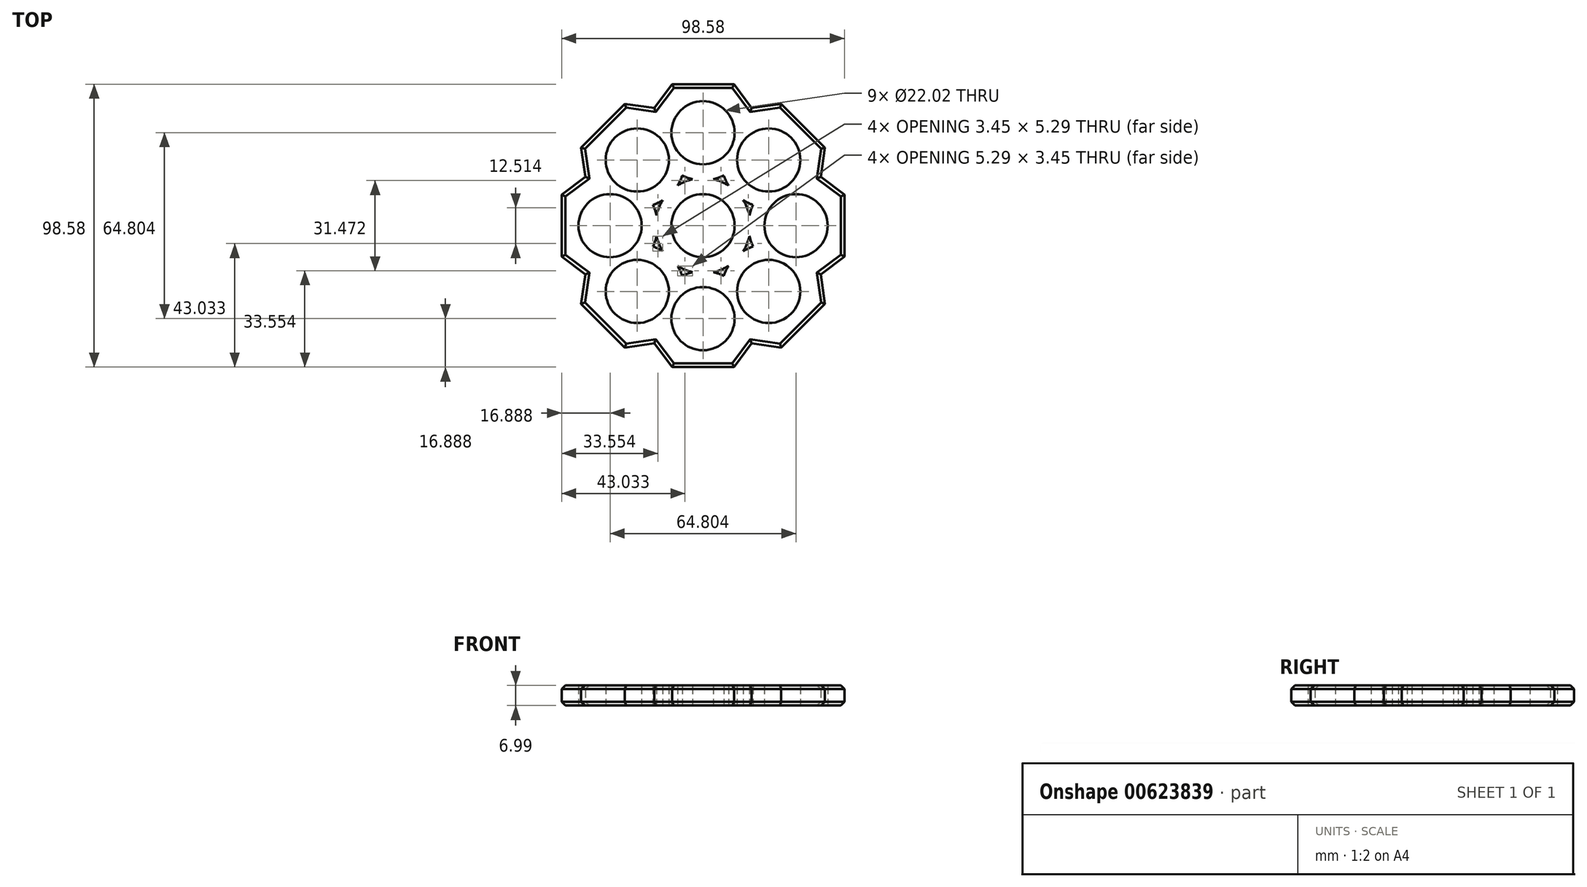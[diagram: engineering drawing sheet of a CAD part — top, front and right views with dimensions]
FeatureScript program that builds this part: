
annotation { "Feature Type Name" : "Feature", "Feature Type Description" : "" }
export const myFeature = defineFeature(function(context is Context, id is Id, definition is map)
    precondition{}
    {
        {
            var Q0;
            Q0=qCreatedBy(makeId("Top.planeOp"),FACE);
            var sketch = newSketch(context, id + "F0", { "sketchPlane" : qUnion([Q0])});
            skLineSegment(sketch, "E0", {"start": v(-9.37, 5.78) * mm, "end": v(-23.41, 32.4) * mm});
            skLineSegment(sketch, "E1", {"start": v(-23.41, 32.4) * mm, "end": v(-10.8, 49.3) * mm});
            skLineSegment(sketch, "E2", {"start": v(-10.8, 49.3) * mm, "end": v(10.8, 49.3) * mm});
            skLineSegment(sketch, "E3", {"start": v(10.8, 49.3) * mm, "end": v(23.41, 32.4) * mm});
            skLineSegment(sketch, "E4", {"start": v(23.41, 32.4) * mm, "end": v(9.37, 5.78) * mm});
            skLineSegment(sketch, "E5", {"start": v(0, 49.3) * mm, "end": v(0, 32.4) * mm});
            skCircle(sketch, "E6", {"center": v(0, 0) * mm, "radius": 11.01 * mm});
            skLineSegment(sketch, "E7", {"start": v(-23.41, 32.4) * mm, "end": v(23.41, 32.4) * mm});
            skLineSegment(sketch, "E8", {"start": v(0, 32.4) * mm, "end": v(0, 0) * mm});
            skCircle(sketch, "E9", {"center": v(0, 32.4) * mm, "radius": 11.01 * mm});
            skLineSegment(sketch, "E10.1.0", {"start": v(-39.47, 6.36) * mm, "end": v(-42.49, 27.22) * mm});
            skLineSegment(sketch, "E10.1.1", {"start": v(-39.47, 6.36) * mm, "end": v(-6.36, 39.47) * mm});
            skLineSegment(sketch, "E10.1.2", {"start": v(-10.71, -2.54) * mm, "end": v(-39.47, 6.36) * mm});
            skLineSegment(sketch, "E10.1.3", {"start": v(-6.36, 39.47) * mm, "end": v(2.54, 10.71) * mm});
            skCircle(sketch, "E10.1.4", {"center": v(-22.91, 22.91) * mm, "radius": 11.01 * mm});
            skLineSegment(sketch, "E10.1.5", {"start": v(-22.91, 22.91) * mm, "end": v(0, 0) * mm});
            skLineSegment(sketch, "E10.1.6", {"start": v(-34.86, 34.86) * mm, "end": v(-22.91, 22.91) * mm});
            skLineSegment(sketch, "E10.1.7", {"start": v(-42.49, 27.22) * mm, "end": v(-27.22, 42.49) * mm});
            skLineSegment(sketch, "E10.1.8", {"start": v(-27.22, 42.49) * mm, "end": v(-6.36, 39.47) * mm});
            skLineSegment(sketch, "E10.2.0", {"start": v(-32.4, -23.41) * mm, "end": v(-49.3, -10.8) * mm});
            skLineSegment(sketch, "E10.2.1", {"start": v(-32.4, -23.41) * mm, "end": v(-32.4, 23.41) * mm});
            skLineSegment(sketch, "E10.2.2", {"start": v(-5.78, -9.37) * mm, "end": v(-32.4, -23.41) * mm});
            skLineSegment(sketch, "E10.2.3", {"start": v(-32.4, 23.41) * mm, "end": v(-5.78, 9.37) * mm});
            skCircle(sketch, "E10.2.4", {"center": v(-32.4, 0) * mm, "radius": 11.01 * mm});
            skLineSegment(sketch, "E10.2.5", {"start": v(-32.4, 0) * mm, "end": v(0, 0) * mm});
            skLineSegment(sketch, "E10.2.6", {"start": v(-49.3, 0) * mm, "end": v(-32.4, 0) * mm});
            skLineSegment(sketch, "E10.2.7", {"start": v(-49.3, -10.8) * mm, "end": v(-49.3, 10.8) * mm});
            skLineSegment(sketch, "E10.2.8", {"start": v(-49.3, 10.8) * mm, "end": v(-32.4, 23.41) * mm});
            skLineSegment(sketch, "E10.3.0", {"start": v(-6.36, -39.47) * mm, "end": v(-27.22, -42.49) * mm});
            skLineSegment(sketch, "E10.3.1", {"start": v(-6.36, -39.47) * mm, "end": v(-39.47, -6.36) * mm});
            skLineSegment(sketch, "E10.3.2", {"start": v(2.54, -10.71) * mm, "end": v(-6.36, -39.47) * mm});
            skLineSegment(sketch, "E10.3.3", {"start": v(-39.47, -6.36) * mm, "end": v(-10.71, 2.54) * mm});
            skCircle(sketch, "E10.3.4", {"center": v(-22.91, -22.91) * mm, "radius": 11.01 * mm});
            skLineSegment(sketch, "E10.3.5", {"start": v(-22.91, -22.91) * mm, "end": v(0, 0) * mm});
            skLineSegment(sketch, "E10.3.6", {"start": v(-34.86, -34.86) * mm, "end": v(-22.91, -22.91) * mm});
            skLineSegment(sketch, "E10.3.7", {"start": v(-27.22, -42.49) * mm, "end": v(-42.49, -27.22) * mm});
            skLineSegment(sketch, "E10.3.8", {"start": v(-42.49, -27.22) * mm, "end": v(-39.47, -6.36) * mm});
            skLineSegment(sketch, "E10.4.0", {"start": v(23.41, -32.4) * mm, "end": v(10.8, -49.3) * mm});
            skLineSegment(sketch, "E10.4.1", {"start": v(23.41, -32.4) * mm, "end": v(-23.41, -32.4) * mm});
            skLineSegment(sketch, "E10.4.2", {"start": v(9.37, -5.78) * mm, "end": v(23.41, -32.4) * mm});
            skLineSegment(sketch, "E10.4.3", {"start": v(-23.41, -32.4) * mm, "end": v(-9.37, -5.78) * mm});
            skCircle(sketch, "E10.4.4", {"center": v(0, -32.4) * mm, "radius": 11.01 * mm});
            skLineSegment(sketch, "E10.4.5", {"start": v(0, -32.4) * mm, "end": v(0, 0) * mm});
            skLineSegment(sketch, "E10.4.6", {"start": v(0, -49.3) * mm, "end": v(0, -32.4) * mm});
            skLineSegment(sketch, "E10.4.7", {"start": v(10.8, -49.3) * mm, "end": v(-10.8, -49.3) * mm});
            skLineSegment(sketch, "E10.4.8", {"start": v(-10.8, -49.3) * mm, "end": v(-23.41, -32.4) * mm});
            skLineSegment(sketch, "E10.5.0", {"start": v(39.47, -6.36) * mm, "end": v(42.49, -27.22) * mm});
            skLineSegment(sketch, "E10.5.1", {"start": v(39.47, -6.36) * mm, "end": v(6.36, -39.47) * mm});
            skLineSegment(sketch, "E10.5.2", {"start": v(10.71, 2.54) * mm, "end": v(39.47, -6.36) * mm});
            skLineSegment(sketch, "E10.5.3", {"start": v(6.36, -39.47) * mm, "end": v(-2.54, -10.71) * mm});
            skCircle(sketch, "E10.5.4", {"center": v(22.91, -22.91) * mm, "radius": 11.01 * mm});
            skLineSegment(sketch, "E10.5.5", {"start": v(22.91, -22.91) * mm, "end": v(0, 0) * mm});
            skLineSegment(sketch, "E10.5.6", {"start": v(34.86, -34.86) * mm, "end": v(22.91, -22.91) * mm});
            skLineSegment(sketch, "E10.5.7", {"start": v(42.49, -27.22) * mm, "end": v(27.22, -42.49) * mm});
            skLineSegment(sketch, "E10.5.8", {"start": v(27.22, -42.49) * mm, "end": v(6.36, -39.47) * mm});
            skLineSegment(sketch, "E10.6.0", {"start": v(32.4, 23.41) * mm, "end": v(49.3, 10.8) * mm});
            skLineSegment(sketch, "E10.6.1", {"start": v(32.4, 23.41) * mm, "end": v(32.4, -23.41) * mm});
            skLineSegment(sketch, "E10.6.2", {"start": v(5.78, 9.37) * mm, "end": v(32.4, 23.41) * mm});
            skLineSegment(sketch, "E10.6.3", {"start": v(32.4, -23.41) * mm, "end": v(5.78, -9.37) * mm});
            skCircle(sketch, "E10.6.4", {"center": v(32.4, 0) * mm, "radius": 11.01 * mm});
            skLineSegment(sketch, "E10.6.5", {"start": v(32.4, 0) * mm, "end": v(0, 0) * mm});
            skLineSegment(sketch, "E10.6.6", {"start": v(49.3, 0) * mm, "end": v(32.4, 0) * mm});
            skLineSegment(sketch, "E10.6.7", {"start": v(49.3, 10.8) * mm, "end": v(49.3, -10.8) * mm});
            skLineSegment(sketch, "E10.6.8", {"start": v(49.3, -10.8) * mm, "end": v(32.4, -23.41) * mm});
            skLineSegment(sketch, "E10.7.0", {"start": v(6.36, 39.47) * mm, "end": v(27.22, 42.49) * mm});
            skLineSegment(sketch, "E10.7.1", {"start": v(6.36, 39.47) * mm, "end": v(39.47, 6.36) * mm});
            skLineSegment(sketch, "E10.7.2", {"start": v(-2.54, 10.71) * mm, "end": v(6.36, 39.47) * mm});
            skLineSegment(sketch, "E10.7.3", {"start": v(39.47, 6.36) * mm, "end": v(10.71, -2.54) * mm});
            skCircle(sketch, "E10.7.4", {"center": v(22.91, 22.91) * mm, "radius": 11.01 * mm});
            skLineSegment(sketch, "E10.7.5", {"start": v(22.91, 22.91) * mm, "end": v(0, 0) * mm});
            skLineSegment(sketch, "E10.7.6", {"start": v(34.86, 34.86) * mm, "end": v(22.91, 22.91) * mm});
            skLineSegment(sketch, "E10.7.7", {"start": v(27.22, 42.49) * mm, "end": v(42.49, 27.22) * mm});
            skLineSegment(sketch, "E10.7.8", {"start": v(42.49, 27.22) * mm, "end": v(39.47, 6.36) * mm});
            skSolve(sketch);
        }
        {
            var Q0;
            {var subQ5=sQuery(id+"F0.wireOp",EDGE,"E10.1.8");var subQ7=sQuery(id+"F0.wireOp",EDGE,"E1");var subQ8=makeQuery(id+"F0.imprint","INTERSECT",VERTEX,{"derivedFrom":[subQ7,subQ5]});Q0=makeQuery(id+"F0.imprint","IMPRINT",FACE,{"disambiguationData":[TD([[makeQuery(id+"F0.imprint","IMPRINT",EDGE,{"disambiguationData":[TD([[subQ8,1.0]])],"derivedFrom":subQ7}),1.0]])]});}
            var Q1;
            {var subQ5=sQuery(id+"F0.wireOp",EDGE,"E2");var subQ6=sQuery(id+"F0.wireOp",EDGE,"E1");var subQ7=makeQuery(id+"F0.imprint","INTERSECT",VERTEX,{"derivedFrom":[subQ6,subQ5]});Q1=makeQuery(id+"F0.imprint","IMPRINT",FACE,{"disambiguationData":[TD([[makeQuery(id+"F0.imprint","IMPRINT",EDGE,{"disambiguationData":[TD([[subQ7,1.0]])],"derivedFrom":subQ6}),-1.0]])]});}
            var Q2;
            {var subQ1=sQuery(id+"F0.wireOp",EDGE,"E2");var subQ5=sQuery(id+"F0.wireOp",EDGE,"E3");var subQ6=makeQuery(id+"F0.imprint","INTERSECT",VERTEX,{"derivedFrom":[subQ1,subQ5]});Q2=makeQuery(id+"F0.imprint","IMPRINT",FACE,{"disambiguationData":[TD([[makeQuery(id+"F0.imprint","IMPRINT",EDGE,{"disambiguationData":[TD([[subQ6,1.0]])],"derivedFrom":subQ1}),-1.0]])]});}
            var Q3;
            {var subQ5=sQuery(id+"F0.wireOp",EDGE,"E3");var subQ7=sQuery(id+"F0.wireOp",EDGE,"E10.7.0");var subQ9=makeQuery(id+"F0.imprint","INTERSECT",VERTEX,{"derivedFrom":[subQ5,subQ7]});Q3=makeQuery(id+"F0.imprint","IMPRINT",FACE,{"disambiguationData":[TD([[makeQuery(id+"F0.imprint","IMPRINT",EDGE,{"disambiguationData":[TD([[subQ9,-1.0]])],"derivedFrom":subQ5}),1.0]])]});}
            var Q4;
            {var subQ5=sQuery(id+"F0.wireOp",EDGE,"E10.2.8");var subQ7=sQuery(id+"F0.wireOp",EDGE,"E10.1.0");var subQ9=makeQuery(id+"F0.imprint","INTERSECT",VERTEX,{"derivedFrom":[subQ7,subQ5]});Q4=makeQuery(id+"F0.imprint","IMPRINT",FACE,{"disambiguationData":[TD([[makeQuery(id+"F0.imprint","IMPRINT",EDGE,{"disambiguationData":[TD([[subQ9,1.0]])],"derivedFrom":subQ7}),1.0]])]});}
            var Q5;
            {var subQ0=sQuery(id+"F0.wireOp",EDGE,"E10.1.7");var subQ7=sQuery(id+"F0.wireOp",EDGE,"E10.1.0");var subQ8=makeQuery(id+"F0.imprint","INTERSECT",VERTEX,{"derivedFrom":[subQ7,subQ0]});Q5=makeQuery(id+"F0.imprint","IMPRINT",FACE,{"disambiguationData":[TD([[makeQuery(id+"F0.imprint","IMPRINT",EDGE,{"disambiguationData":[TD([[subQ8,1.0]])],"derivedFrom":subQ7}),-1.0]])]});}
            var Q6;
            {var subQ5=sQuery(id+"F0.wireOp",EDGE,"E10.3.8");var subQ7=sQuery(id+"F0.wireOp",EDGE,"E10.2.0");var subQ9=makeQuery(id+"F0.imprint","INTERSECT",VERTEX,{"derivedFrom":[subQ7,subQ5]});Q6=makeQuery(id+"F0.imprint","IMPRINT",FACE,{"disambiguationData":[TD([[makeQuery(id+"F0.imprint","IMPRINT",EDGE,{"disambiguationData":[TD([[subQ9,1.0]])],"derivedFrom":subQ7}),1.0]])]});}
            var Q7;
            {var subQ0=sQuery(id+"F0.wireOp",EDGE,"E10.2.7");var subQ7=sQuery(id+"F0.wireOp",EDGE,"E10.2.0");var subQ8=makeQuery(id+"F0.imprint","INTERSECT",VERTEX,{"derivedFrom":[subQ7,subQ0]});Q7=makeQuery(id+"F0.imprint","IMPRINT",FACE,{"disambiguationData":[TD([[makeQuery(id+"F0.imprint","IMPRINT",EDGE,{"disambiguationData":[TD([[subQ8,1.0]])],"derivedFrom":subQ7}),-1.0]])]});}
            var Q8;
            {var subQ5=sQuery(id+"F0.wireOp",EDGE,"E10.4.8");var subQ7=sQuery(id+"F0.wireOp",EDGE,"E10.3.0");var subQ9=makeQuery(id+"F0.imprint","INTERSECT",VERTEX,{"derivedFrom":[subQ7,subQ5]});Q8=makeQuery(id+"F0.imprint","IMPRINT",FACE,{"disambiguationData":[TD([[makeQuery(id+"F0.imprint","IMPRINT",EDGE,{"disambiguationData":[TD([[subQ9,1.0]])],"derivedFrom":subQ7}),1.0]])]});}
            var Q9;
            {var subQ0=sQuery(id+"F0.wireOp",EDGE,"E10.3.7");var subQ7=sQuery(id+"F0.wireOp",EDGE,"E10.3.0");var subQ8=makeQuery(id+"F0.imprint","INTERSECT",VERTEX,{"derivedFrom":[subQ7,subQ0]});Q9=makeQuery(id+"F0.imprint","IMPRINT",FACE,{"disambiguationData":[TD([[makeQuery(id+"F0.imprint","IMPRINT",EDGE,{"disambiguationData":[TD([[subQ8,1.0]])],"derivedFrom":subQ7}),-1.0]])]});}
            var Q10;
            {var subQ5=sQuery(id+"F0.wireOp",EDGE,"E10.5.8");var subQ7=sQuery(id+"F0.wireOp",EDGE,"E10.4.0");var subQ9=makeQuery(id+"F0.imprint","INTERSECT",VERTEX,{"derivedFrom":[subQ7,subQ5]});Q10=makeQuery(id+"F0.imprint","IMPRINT",FACE,{"disambiguationData":[TD([[makeQuery(id+"F0.imprint","IMPRINT",EDGE,{"disambiguationData":[TD([[subQ9,1.0]])],"derivedFrom":subQ7}),1.0]])]});}
            var Q11;
            {var subQ0=sQuery(id+"F0.wireOp",EDGE,"E10.4.7");var subQ7=sQuery(id+"F0.wireOp",EDGE,"E10.4.0");var subQ8=makeQuery(id+"F0.imprint","INTERSECT",VERTEX,{"derivedFrom":[subQ7,subQ0]});Q11=makeQuery(id+"F0.imprint","IMPRINT",FACE,{"disambiguationData":[TD([[makeQuery(id+"F0.imprint","IMPRINT",EDGE,{"disambiguationData":[TD([[subQ8,1.0]])],"derivedFrom":subQ7}),-1.0]])]});}
            var Q12;
            {var subQ5=sQuery(id+"F0.wireOp",EDGE,"E10.6.8");var subQ7=sQuery(id+"F0.wireOp",EDGE,"E10.5.0");var subQ9=makeQuery(id+"F0.imprint","INTERSECT",VERTEX,{"derivedFrom":[subQ7,subQ5]});Q12=makeQuery(id+"F0.imprint","IMPRINT",FACE,{"disambiguationData":[TD([[makeQuery(id+"F0.imprint","IMPRINT",EDGE,{"disambiguationData":[TD([[subQ9,1.0]])],"derivedFrom":subQ7}),1.0]])]});}
            var Q13;
            {var subQ0=sQuery(id+"F0.wireOp",EDGE,"E10.5.7");var subQ7=sQuery(id+"F0.wireOp",EDGE,"E10.5.0");var subQ8=makeQuery(id+"F0.imprint","INTERSECT",VERTEX,{"derivedFrom":[subQ7,subQ0]});Q13=makeQuery(id+"F0.imprint","IMPRINT",FACE,{"disambiguationData":[TD([[makeQuery(id+"F0.imprint","IMPRINT",EDGE,{"disambiguationData":[TD([[subQ8,1.0]])],"derivedFrom":subQ7}),-1.0]])]});}
            var Q14;
            {var subQ5=sQuery(id+"F0.wireOp",EDGE,"E10.7.8");var subQ7=sQuery(id+"F0.wireOp",EDGE,"E10.6.0");var subQ9=makeQuery(id+"F0.imprint","INTERSECT",VERTEX,{"derivedFrom":[subQ7,subQ5]});Q14=makeQuery(id+"F0.imprint","IMPRINT",FACE,{"disambiguationData":[TD([[makeQuery(id+"F0.imprint","IMPRINT",EDGE,{"disambiguationData":[TD([[subQ9,1.0]])],"derivedFrom":subQ7}),1.0]])]});}
            var Q15;
            {var subQ0=sQuery(id+"F0.wireOp",EDGE,"E10.6.7");var subQ7=sQuery(id+"F0.wireOp",EDGE,"E10.6.0");var subQ8=makeQuery(id+"F0.imprint","INTERSECT",VERTEX,{"derivedFrom":[subQ7,subQ0]});Q15=makeQuery(id+"F0.imprint","IMPRINT",FACE,{"disambiguationData":[TD([[makeQuery(id+"F0.imprint","IMPRINT",EDGE,{"disambiguationData":[TD([[subQ8,1.0]])],"derivedFrom":subQ7}),-1.0]])]});}
            var Q16;
            {var subQ6=sQuery(id+"F0.wireOp",EDGE,"E1");var subQ9=sQuery(id+"F0.wireOp",EDGE,"E10.1.8");var subQ11=makeQuery(id+"F0.imprint","INTERSECT",VERTEX,{"derivedFrom":[subQ6,subQ9]});Q16=makeQuery(id+"F0.imprint","IMPRINT",FACE,{"disambiguationData":[TD([[makeQuery(id+"F0.imprint","IMPRINT",EDGE,{"disambiguationData":[TD([[subQ11,1.0]])],"derivedFrom":subQ6}),-1.0]])]});}
            var Q17;
            {var subQ0=sQuery(id+"F0.wireOp",EDGE,"E10.7.0");var subQ1=sQuery(id+"F0.wireOp",EDGE,"E3");var subQ2=makeQuery(id+"F0.imprint","INTERSECT",VERTEX,{"derivedFrom":[subQ1,subQ0]});Q17=makeQuery(id+"F0.imprint","IMPRINT",FACE,{"disambiguationData":[TD([[makeQuery(id+"F0.imprint","IMPRINT",EDGE,{"disambiguationData":[TD([[subQ2,-1.0]])],"derivedFrom":subQ1}),-1.0]])]});}
            var Q18;
            {var subQ6=sQuery(id+"F0.wireOp",EDGE,"E10.1.0");var subQ9=sQuery(id+"F0.wireOp",EDGE,"E10.2.8");var subQ11=makeQuery(id+"F0.imprint","INTERSECT",VERTEX,{"derivedFrom":[subQ6,subQ9]});Q18=makeQuery(id+"F0.imprint","IMPRINT",FACE,{"disambiguationData":[TD([[makeQuery(id+"F0.imprint","IMPRINT",EDGE,{"disambiguationData":[TD([[subQ11,1.0]])],"derivedFrom":subQ6}),-1.0]])]});}
            var Q19;
            {var subQ6=sQuery(id+"F0.wireOp",EDGE,"E10.2.0");var subQ9=sQuery(id+"F0.wireOp",EDGE,"E10.3.8");var subQ11=makeQuery(id+"F0.imprint","INTERSECT",VERTEX,{"derivedFrom":[subQ6,subQ9]});Q19=makeQuery(id+"F0.imprint","IMPRINT",FACE,{"disambiguationData":[TD([[makeQuery(id+"F0.imprint","IMPRINT",EDGE,{"disambiguationData":[TD([[subQ11,1.0]])],"derivedFrom":subQ6}),-1.0]])]});}
            var Q20;
            {var subQ6=sQuery(id+"F0.wireOp",EDGE,"E10.4.0");var subQ9=sQuery(id+"F0.wireOp",EDGE,"E10.5.8");var subQ11=makeQuery(id+"F0.imprint","INTERSECT",VERTEX,{"derivedFrom":[subQ6,subQ9]});Q20=makeQuery(id+"F0.imprint","IMPRINT",FACE,{"disambiguationData":[TD([[makeQuery(id+"F0.imprint","IMPRINT",EDGE,{"disambiguationData":[TD([[subQ11,1.0]])],"derivedFrom":subQ6}),-1.0]])]});}
            var Q21;
            {var subQ6=sQuery(id+"F0.wireOp",EDGE,"E10.5.0");var subQ9=sQuery(id+"F0.wireOp",EDGE,"E10.6.8");var subQ11=makeQuery(id+"F0.imprint","INTERSECT",VERTEX,{"derivedFrom":[subQ6,subQ9]});Q21=makeQuery(id+"F0.imprint","IMPRINT",FACE,{"disambiguationData":[TD([[makeQuery(id+"F0.imprint","IMPRINT",EDGE,{"disambiguationData":[TD([[subQ11,1.0]])],"derivedFrom":subQ6}),-1.0]])]});}
            var Q22;
            {var subQ6=sQuery(id+"F0.wireOp",EDGE,"E10.6.0");var subQ9=sQuery(id+"F0.wireOp",EDGE,"E10.7.8");var subQ11=makeQuery(id+"F0.imprint","INTERSECT",VERTEX,{"derivedFrom":[subQ6,subQ9]});Q22=makeQuery(id+"F0.imprint","IMPRINT",FACE,{"disambiguationData":[TD([[makeQuery(id+"F0.imprint","IMPRINT",EDGE,{"disambiguationData":[TD([[subQ11,1.0]])],"derivedFrom":subQ6}),-1.0]])]});}
            var Q23;
            {var subQ5=sQuery(id+"F0.wireOp",EDGE,"E10.1.3");var subQ6=sQuery(id+"F0.wireOp",EDGE,"E6");var subQ7=makeQuery(id+"F0.imprint","INTERSECT",VERTEX,{"derivedFrom":[subQ6,subQ5]});Q23=makeQuery(id+"F0.imprint","IMPRINT",FACE,{"disambiguationData":[TD([[makeQuery(id+"F0.imprint","IMPRINT",EDGE,{"disambiguationData":[TD([[subQ7,1.0]])],"derivedFrom":subQ6}),-1.0]])]});}
            var Q24;
            {var subQ8=sQuery(id+"F0.wireOp",EDGE,"E6");var subQ11=sQuery(id+"F0.wireOp",EDGE,"E4");var subQ12=makeQuery(id+"F0.imprint","INTERSECT",VERTEX,{"derivedFrom":[subQ11,subQ8]});Q24=makeQuery(id+"F0.imprint","IMPRINT",FACE,{"disambiguationData":[TD([[makeQuery(id+"F0.imprint","IMPRINT",EDGE,{"disambiguationData":[TD([[subQ12,1.0]])],"derivedFrom":subQ8}),-1.0]])]});}
            var Q25;
            {var subQ12=sQuery(id+"F0.wireOp",EDGE,"E6");var subQ14=sQuery(id+"F0.wireOp",EDGE,"E10.4.2");var subQ15=makeQuery(id+"F0.imprint","INTERSECT",VERTEX,{"derivedFrom":[subQ12,subQ14]});Q25=makeQuery(id+"F0.imprint","IMPRINT",FACE,{"disambiguationData":[TD([[makeQuery(id+"F0.imprint","IMPRINT",EDGE,{"disambiguationData":[TD([[subQ15,-1.0]])],"derivedFrom":subQ12}),-1.0]])]});}
            var Q26;
            {var subQ5=sQuery(id+"F0.wireOp",EDGE,"E10.3.2");var subQ6=sQuery(id+"F0.wireOp",EDGE,"E6");var subQ7=makeQuery(id+"F0.imprint","INTERSECT",VERTEX,{"derivedFrom":[subQ6,subQ5]});Q26=makeQuery(id+"F0.imprint","IMPRINT",FACE,{"disambiguationData":[TD([[makeQuery(id+"F0.imprint","IMPRINT",EDGE,{"disambiguationData":[TD([[subQ7,-1.0]])],"derivedFrom":subQ6}),-1.0]])]});}
            var Q27;
            {var subQ5=sQuery(id+"F0.wireOp",EDGE,"E10.2.2");var subQ6=sQuery(id+"F0.wireOp",EDGE,"E6");var subQ7=makeQuery(id+"F0.imprint","INTERSECT",VERTEX,{"derivedFrom":[subQ6,subQ5]});Q27=makeQuery(id+"F0.imprint","IMPRINT",FACE,{"disambiguationData":[TD([[makeQuery(id+"F0.imprint","IMPRINT",EDGE,{"disambiguationData":[TD([[subQ7,-1.0]])],"derivedFrom":subQ6}),-1.0]])]});}
            var Q28;
            {var subQ8=sQuery(id+"F0.wireOp",EDGE,"E6");var subQ12=sQuery(id+"F0.wireOp",EDGE,"E0");var subQ13=makeQuery(id+"F0.imprint","INTERSECT",VERTEX,{"derivedFrom":[subQ12,subQ8]});Q28=makeQuery(id+"F0.imprint","IMPRINT",FACE,{"disambiguationData":[TD([[makeQuery(id+"F0.imprint","IMPRINT",EDGE,{"disambiguationData":[TD([[subQ13,-1.0]])],"derivedFrom":subQ8}),-1.0]])]});}
            var Q29;
            {var subQ5=sQuery(id+"F0.wireOp",EDGE,"E10.2.3");var subQ6=sQuery(id+"F0.wireOp",EDGE,"E6");var subQ7=makeQuery(id+"F0.imprint","INTERSECT",VERTEX,{"derivedFrom":[subQ6,subQ5]});Q29=makeQuery(id+"F0.imprint","IMPRINT",FACE,{"disambiguationData":[TD([[makeQuery(id+"F0.imprint","IMPRINT",EDGE,{"disambiguationData":[TD([[subQ7,1.0]])],"derivedFrom":subQ6}),-1.0]])]});}
            var Q30;
            {var subQ0=sQuery(id+"F0.wireOp",EDGE,"E10.2.1");var subQ1=sQuery(id+"F0.wireOp",EDGE,"E10.1.1");var subQ2=makeQuery(id+"F0.imprint","INTERSECT",VERTEX,{"derivedFrom":[subQ1,subQ0]});Q30=makeQuery(id+"F0.imprint","IMPRINT",FACE,{"disambiguationData":[TD([[makeQuery(id+"F0.imprint","IMPRINT",EDGE,{"disambiguationData":[TD([[subQ2,-1.0]])],"derivedFrom":subQ1}),1.0]])]});}
            var Q31;
            {var subQ0=sQuery(id+"F0.wireOp",EDGE,"E10.2.4");var subQ1=sQuery(id+"F0.wireOp",EDGE,"E10.1.1");var subQ2=makeQuery(id+"F0.imprint","INTERSECT",VERTEX,{"derivedFrom":[subQ1,subQ0]});Q31=makeQuery(id+"F0.imprint","IMPRINT",FACE,{"disambiguationData":[TD([[makeQuery(id+"F0.imprint","IMPRINT",EDGE,{"disambiguationData":[TD([[subQ2,-1.0]])],"derivedFrom":subQ1}),-1.0]])]});}
            var Q32;
            {var subQ0=sQuery(id+"F0.wireOp",EDGE,"E10.3.1");var subQ1=sQuery(id+"F0.wireOp",EDGE,"E10.2.1");var subQ2=makeQuery(id+"F0.imprint","INTERSECT",VERTEX,{"derivedFrom":[subQ1,subQ0]});Q32=makeQuery(id+"F0.imprint","IMPRINT",FACE,{"disambiguationData":[TD([[makeQuery(id+"F0.imprint","IMPRINT",EDGE,{"disambiguationData":[TD([[subQ2,-1.0]])],"derivedFrom":subQ1}),1.0]])]});}
            var Q33;
            {var subQ0=sQuery(id+"F0.wireOp",EDGE,"E10.1.1");var subQ1=sQuery(id+"F0.wireOp",EDGE,"E7");var subQ2=makeQuery(id+"F0.imprint","INTERSECT",VERTEX,{"derivedFrom":[subQ1,subQ0]});Q33=makeQuery(id+"F0.imprint","IMPRINT",FACE,{"disambiguationData":[TD([[makeQuery(id+"F0.imprint","IMPRINT",EDGE,{"disambiguationData":[TD([[subQ2,-1.0]])],"derivedFrom":subQ1}),1.0]])]});}
            var Q34;
            {var subQ0=sQuery(id+"F0.wireOp",EDGE,"E10.1.4");var subQ1=sQuery(id+"F0.wireOp",EDGE,"E7");var subQ2=makeQuery(id+"F0.imprint","INTERSECT",VERTEX,{"derivedFrom":[subQ1,subQ0]});Q34=makeQuery(id+"F0.imprint","IMPRINT",FACE,{"disambiguationData":[TD([[makeQuery(id+"F0.imprint","IMPRINT",EDGE,{"disambiguationData":[TD([[subQ2,-1.0]])],"derivedFrom":subQ1}),-1.0]])]});}
            var Q35;
            {var subQ0=sQuery(id+"F0.wireOp",EDGE,"E10.2.4");var subQ1=sQuery(id+"F0.wireOp",EDGE,"E10.1.2");var subQ2=makeQuery(id+"F0.imprint","INTERSECT",VERTEX,{"derivedFrom":[subQ1,subQ0]});Q35=makeQuery(id+"F0.imprint","IMPRINT",FACE,{"disambiguationData":[TD([[makeQuery(id+"F0.imprint","IMPRINT",EDGE,{"disambiguationData":[TD([[subQ2,1.0]])],"derivedFrom":subQ0}),-1.0]])]});}
            var Q36;
            {var subQ0=sQuery(id+"F0.wireOp",EDGE,"E10.2.3");var subQ1=sQuery(id+"F0.wireOp",EDGE,"E10.1.4");var subQ2=makeQuery(id+"F0.imprint","INTERSECT",VERTEX,{"derivedFrom":[subQ1,subQ0]});Q36=makeQuery(id+"F0.imprint","IMPRINT",FACE,{"disambiguationData":[TD([[makeQuery(id+"F0.imprint","IMPRINT",EDGE,{"disambiguationData":[TD([[subQ2,-1.0]])],"derivedFrom":subQ1}),-1.0]])]});}
            var Q37;
            {var subQ0=sQuery(id+"F0.wireOp",EDGE,"E10.1.4");var subQ1=sQuery(id+"F0.wireOp",EDGE,"E0");var subQ2=makeQuery(id+"F0.imprint","INTERSECT",VERTEX,{"derivedFrom":[subQ1,subQ0]});Q37=makeQuery(id+"F0.imprint","IMPRINT",FACE,{"disambiguationData":[TD([[makeQuery(id+"F0.imprint","IMPRINT",EDGE,{"disambiguationData":[TD([[subQ2,1.0]])],"derivedFrom":subQ0}),-1.0]])]});}
            var Q38;
            {var subQ0=sQuery(id+"F0.wireOp",EDGE,"E9");var subQ1=sQuery(id+"F0.wireOp",EDGE,"E8");var subQ2=makeQuery(id+"F0.imprint","INTERSECT",VERTEX,{"derivedFrom":[subQ1,subQ0]});Q38=makeQuery(id+"F0.imprint","IMPRINT",FACE,{"disambiguationData":[TD([[makeQuery(id+"F0.imprint","IMPRINT",EDGE,{"disambiguationData":[TD([[subQ2,-1.0]])],"derivedFrom":subQ0}),-1.0]])]});}
            var Q39;
            {var subQ0=sQuery(id+"F0.wireOp",EDGE,"E9");var subQ1=sQuery(id+"F0.wireOp",EDGE,"E8");var subQ2=makeQuery(id+"F0.imprint","INTERSECT",VERTEX,{"derivedFrom":[subQ1,subQ0]});Q39=makeQuery(id+"F0.imprint","IMPRINT",FACE,{"disambiguationData":[TD([[makeQuery(id+"F0.imprint","IMPRINT",EDGE,{"disambiguationData":[TD([[subQ2,1.0]])],"derivedFrom":subQ0}),-1.0]])]});}
            var Q40;
            {var subQ0=sQuery(id+"F0.wireOp",EDGE,"E9");var subQ1=sQuery(id+"F0.wireOp",EDGE,"E7");var subQ2=makeQuery(id+"F0.imprint","INTERSECT",VERTEX,{"disambiguationData":[OD(1.0)],"derivedFrom":[subQ1,subQ0]});Q40=makeQuery(id+"F0.imprint","IMPRINT",FACE,{"disambiguationData":[TD([[makeQuery(id+"F0.imprint","IMPRINT",EDGE,{"disambiguationData":[TD([[subQ2,-1.0]])],"derivedFrom":subQ1}),1.0]])]});}
            var Q41;
            {var subQ0=sQuery(id+"F0.wireOp",EDGE,"E10.7.1");var subQ1=sQuery(id+"F0.wireOp",EDGE,"E7");var subQ2=makeQuery(id+"F0.imprint","INTERSECT",VERTEX,{"derivedFrom":[subQ1,subQ0]});Q41=makeQuery(id+"F0.imprint","IMPRINT",FACE,{"disambiguationData":[TD([[makeQuery(id+"F0.imprint","IMPRINT",EDGE,{"disambiguationData":[TD([[subQ2,-1.0]])],"derivedFrom":subQ1}),-1.0]])]});}
            var Q42;
            {var subQ0=sQuery(id+"F0.wireOp",EDGE,"E10.7.4");var subQ1=sQuery(id+"F0.wireOp",EDGE,"E10.6.2");var subQ2=makeQuery(id+"F0.imprint","INTERSECT",VERTEX,{"derivedFrom":[subQ1,subQ0]});Q42=makeQuery(id+"F0.imprint","IMPRINT",FACE,{"disambiguationData":[TD([[makeQuery(id+"F0.imprint","IMPRINT",EDGE,{"disambiguationData":[TD([[subQ2,1.0]])],"derivedFrom":subQ0}),-1.0]])]});}
            var Q43;
            {var subQ0=sQuery(id+"F0.wireOp",EDGE,"E10.7.1");var subQ1=sQuery(id+"F0.wireOp",EDGE,"E10.6.1");var subQ2=makeQuery(id+"F0.imprint","INTERSECT",VERTEX,{"derivedFrom":[subQ1,subQ0]});Q43=makeQuery(id+"F0.imprint","IMPRINT",FACE,{"disambiguationData":[TD([[makeQuery(id+"F0.imprint","IMPRINT",EDGE,{"disambiguationData":[TD([[subQ2,-1.0]])],"derivedFrom":subQ1}),1.0]])]});}
            var Q44;
            {var subQ0=sQuery(id+"F0.wireOp",EDGE,"E10.7.4");var subQ1=sQuery(id+"F0.wireOp",EDGE,"E10.6.1");var subQ2=makeQuery(id+"F0.imprint","INTERSECT",VERTEX,{"derivedFrom":[subQ1,subQ0]});Q44=makeQuery(id+"F0.imprint","IMPRINT",FACE,{"disambiguationData":[TD([[makeQuery(id+"F0.imprint","IMPRINT",EDGE,{"disambiguationData":[TD([[subQ2,-1.0]])],"derivedFrom":subQ1}),-1.0]])]});}
            var Q45;
            {var subQ0=sQuery(id+"F0.wireOp",EDGE,"E10.7.4");var subQ1=sQuery(id+"F0.wireOp",EDGE,"E4");var subQ2=makeQuery(id+"F0.imprint","INTERSECT",VERTEX,{"derivedFrom":[subQ1,subQ0]});Q45=makeQuery(id+"F0.imprint","IMPRINT",FACE,{"disambiguationData":[TD([[makeQuery(id+"F0.imprint","IMPRINT",EDGE,{"disambiguationData":[TD([[subQ2,-1.0]])],"derivedFrom":subQ0}),-1.0]])]});}
            var Q46;
            {var subQ0=sQuery(id+"F0.wireOp",EDGE,"E10.6.4");var subQ1=sQuery(id+"F0.wireOp",EDGE,"E10.5.2");var subQ2=makeQuery(id+"F0.imprint","INTERSECT",VERTEX,{"derivedFrom":[subQ1,subQ0]});Q46=makeQuery(id+"F0.imprint","IMPRINT",FACE,{"disambiguationData":[TD([[makeQuery(id+"F0.imprint","IMPRINT",EDGE,{"disambiguationData":[TD([[subQ2,1.0]])],"derivedFrom":subQ0}),-1.0]])]});}
            var Q47;
            {var subQ0=sQuery(id+"F0.wireOp",EDGE,"E10.7.3");var subQ1=sQuery(id+"F0.wireOp",EDGE,"E10.6.4");var subQ2=makeQuery(id+"F0.imprint","INTERSECT",VERTEX,{"derivedFrom":[subQ1,subQ0]});Q47=makeQuery(id+"F0.imprint","IMPRINT",FACE,{"disambiguationData":[TD([[makeQuery(id+"F0.imprint","IMPRINT",EDGE,{"disambiguationData":[TD([[subQ2,-1.0]])],"derivedFrom":subQ1}),-1.0]])]});}
            var Q48;
            {var subQ0=sQuery(id+"F0.wireOp",EDGE,"E10.6.4");var subQ1=sQuery(id+"F0.wireOp",EDGE,"E10.5.1");var subQ2=makeQuery(id+"F0.imprint","INTERSECT",VERTEX,{"derivedFrom":[subQ1,subQ0]});Q48=makeQuery(id+"F0.imprint","IMPRINT",FACE,{"disambiguationData":[TD([[makeQuery(id+"F0.imprint","IMPRINT",EDGE,{"disambiguationData":[TD([[subQ2,-1.0]])],"derivedFrom":subQ1}),-1.0]])]});}
            var Q49;
            {var subQ0=sQuery(id+"F0.wireOp",EDGE,"E10.6.1");var subQ1=sQuery(id+"F0.wireOp",EDGE,"E10.5.1");var subQ2=makeQuery(id+"F0.imprint","INTERSECT",VERTEX,{"derivedFrom":[subQ1,subQ0]});Q49=makeQuery(id+"F0.imprint","IMPRINT",FACE,{"disambiguationData":[TD([[makeQuery(id+"F0.imprint","IMPRINT",EDGE,{"disambiguationData":[TD([[subQ2,-1.0]])],"derivedFrom":subQ1}),1.0]])]});}
            var Q50;
            {var subQ0=sQuery(id+"F0.wireOp",EDGE,"E10.5.4");var subQ1=sQuery(id+"F0.wireOp",EDGE,"E10.4.1");var subQ2=makeQuery(id+"F0.imprint","INTERSECT",VERTEX,{"derivedFrom":[subQ1,subQ0]});Q50=makeQuery(id+"F0.imprint","IMPRINT",FACE,{"disambiguationData":[TD([[makeQuery(id+"F0.imprint","IMPRINT",EDGE,{"disambiguationData":[TD([[subQ2,-1.0]])],"derivedFrom":subQ1}),-1.0]])]});}
            var Q51;
            {var subQ0=sQuery(id+"F0.wireOp",EDGE,"E10.5.1");var subQ1=sQuery(id+"F0.wireOp",EDGE,"E10.4.1");var subQ2=makeQuery(id+"F0.imprint","INTERSECT",VERTEX,{"derivedFrom":[subQ1,subQ0]});Q51=makeQuery(id+"F0.imprint","IMPRINT",FACE,{"disambiguationData":[TD([[makeQuery(id+"F0.imprint","IMPRINT",EDGE,{"disambiguationData":[TD([[subQ2,-1.0]])],"derivedFrom":subQ1}),1.0]])]});}
            var Q52;
            {var subQ0=sQuery(id+"F0.wireOp",EDGE,"E10.6.3");var subQ1=sQuery(id+"F0.wireOp",EDGE,"E10.5.4");var subQ2=makeQuery(id+"F0.imprint","INTERSECT",VERTEX,{"derivedFrom":[subQ1,subQ0]});Q52=makeQuery(id+"F0.imprint","IMPRINT",FACE,{"disambiguationData":[TD([[makeQuery(id+"F0.imprint","IMPRINT",EDGE,{"disambiguationData":[TD([[subQ2,-1.0]])],"derivedFrom":subQ1}),-1.0]])]});}
            var Q53;
            {var subQ0=sQuery(id+"F0.wireOp",EDGE,"E10.5.4");var subQ1=sQuery(id+"F0.wireOp",EDGE,"E10.4.2");var subQ2=makeQuery(id+"F0.imprint","INTERSECT",VERTEX,{"derivedFrom":[subQ1,subQ0]});Q53=makeQuery(id+"F0.imprint","IMPRINT",FACE,{"disambiguationData":[TD([[makeQuery(id+"F0.imprint","IMPRINT",EDGE,{"disambiguationData":[TD([[subQ2,1.0]])],"derivedFrom":subQ0}),-1.0]])]});}
            var Q54;
            {var subQ0=sQuery(id+"F0.wireOp",EDGE,"E10.5.3");var subQ1=sQuery(id+"F0.wireOp",EDGE,"E10.4.4");var subQ2=makeQuery(id+"F0.imprint","INTERSECT",VERTEX,{"derivedFrom":[subQ1,subQ0]});Q54=makeQuery(id+"F0.imprint","IMPRINT",FACE,{"disambiguationData":[TD([[makeQuery(id+"F0.imprint","IMPRINT",EDGE,{"disambiguationData":[TD([[subQ2,-1.0]])],"derivedFrom":subQ1}),-1.0]])]});}
            var Q55;
            {var subQ0=sQuery(id+"F0.wireOp",EDGE,"E10.4.4");var subQ1=sQuery(id+"F0.wireOp",EDGE,"E10.3.2");var subQ2=makeQuery(id+"F0.imprint","INTERSECT",VERTEX,{"derivedFrom":[subQ1,subQ0]});Q55=makeQuery(id+"F0.imprint","IMPRINT",FACE,{"disambiguationData":[TD([[makeQuery(id+"F0.imprint","IMPRINT",EDGE,{"disambiguationData":[TD([[subQ2,1.0]])],"derivedFrom":subQ0}),-1.0]])]});}
            var Q56;
            {var subQ6=sQuery(id+"F0.wireOp",EDGE,"E10.3.0");var subQ9=sQuery(id+"F0.wireOp",EDGE,"E10.4.8");var subQ11=makeQuery(id+"F0.imprint","INTERSECT",VERTEX,{"derivedFrom":[subQ6,subQ9]});Q56=makeQuery(id+"F0.imprint","IMPRINT",FACE,{"disambiguationData":[TD([[makeQuery(id+"F0.imprint","IMPRINT",EDGE,{"disambiguationData":[TD([[subQ11,1.0]])],"derivedFrom":subQ6}),-1.0]])]});}
            var Q57;
            {var subQ0=sQuery(id+"F0.wireOp",EDGE,"E10.4.4");var subQ1=sQuery(id+"F0.wireOp",EDGE,"E10.3.1");var subQ2=makeQuery(id+"F0.imprint","INTERSECT",VERTEX,{"derivedFrom":[subQ1,subQ0]});Q57=makeQuery(id+"F0.imprint","IMPRINT",FACE,{"disambiguationData":[TD([[makeQuery(id+"F0.imprint","IMPRINT",EDGE,{"disambiguationData":[TD([[subQ2,-1.0]])],"derivedFrom":subQ1}),-1.0]])]});}
            var Q58;
            {var subQ0=sQuery(id+"F0.wireOp",EDGE,"E10.4.1");var subQ1=sQuery(id+"F0.wireOp",EDGE,"E10.3.1");var subQ2=makeQuery(id+"F0.imprint","INTERSECT",VERTEX,{"derivedFrom":[subQ1,subQ0]});Q58=makeQuery(id+"F0.imprint","IMPRINT",FACE,{"disambiguationData":[TD([[makeQuery(id+"F0.imprint","IMPRINT",EDGE,{"disambiguationData":[TD([[subQ2,-1.0]])],"derivedFrom":subQ1}),1.0]])]});}
            var Q59;
            {var subQ0=sQuery(id+"F0.wireOp",EDGE,"E10.4.3");var subQ1=sQuery(id+"F0.wireOp",EDGE,"E10.3.4");var subQ2=makeQuery(id+"F0.imprint","INTERSECT",VERTEX,{"derivedFrom":[subQ1,subQ0]});Q59=makeQuery(id+"F0.imprint","IMPRINT",FACE,{"disambiguationData":[TD([[makeQuery(id+"F0.imprint","IMPRINT",EDGE,{"disambiguationData":[TD([[subQ2,-1.0]])],"derivedFrom":subQ1}),-1.0]])]});}
            var Q60;
            {var subQ0=sQuery(id+"F0.wireOp",EDGE,"E10.3.4");var subQ1=sQuery(id+"F0.wireOp",EDGE,"E10.2.2");var subQ2=makeQuery(id+"F0.imprint","INTERSECT",VERTEX,{"derivedFrom":[subQ1,subQ0]});Q60=makeQuery(id+"F0.imprint","IMPRINT",FACE,{"disambiguationData":[TD([[makeQuery(id+"F0.imprint","IMPRINT",EDGE,{"disambiguationData":[TD([[subQ2,1.0]])],"derivedFrom":subQ0}),-1.0]])]});}
            var Q61;
            {var subQ0=sQuery(id+"F0.wireOp",EDGE,"E10.3.4");var subQ1=sQuery(id+"F0.wireOp",EDGE,"E10.2.1");var subQ2=makeQuery(id+"F0.imprint","INTERSECT",VERTEX,{"derivedFrom":[subQ1,subQ0]});Q61=makeQuery(id+"F0.imprint","IMPRINT",FACE,{"disambiguationData":[TD([[makeQuery(id+"F0.imprint","IMPRINT",EDGE,{"disambiguationData":[TD([[subQ2,-1.0]])],"derivedFrom":subQ1}),-1.0]])]});}
            var Q62;
            {var subQ0=sQuery(id+"F0.wireOp",EDGE,"E10.3.3");var subQ1=sQuery(id+"F0.wireOp",EDGE,"E10.2.4");var subQ2=makeQuery(id+"F0.imprint","INTERSECT",VERTEX,{"derivedFrom":[subQ1,subQ0]});Q62=makeQuery(id+"F0.imprint","IMPRINT",FACE,{"disambiguationData":[TD([[makeQuery(id+"F0.imprint","IMPRINT",EDGE,{"disambiguationData":[TD([[subQ2,-1.0]])],"derivedFrom":subQ1}),-1.0]])]});}
            var Q63;
            {var subQ0=sQuery(id+"F0.wireOp",EDGE,"E6");var subQ1=sQuery(id+"F0.wireOp",EDGE,"E4");var subQ2=makeQuery(id+"F0.imprint","INTERSECT",VERTEX,{"derivedFrom":[subQ1,subQ0]});Q63=makeQuery(id+"F0.imprint","IMPRINT",FACE,{"disambiguationData":[TD([[makeQuery(id+"F0.imprint","IMPRINT",EDGE,{"disambiguationData":[TD([[subQ2,-1.0]])],"derivedFrom":subQ0}),-1.0]])]});}
            var Q64;
            {var subQ0=sQuery(id+"F0.wireOp",EDGE,"E10.6.2");var subQ1=sQuery(id+"F0.wireOp",EDGE,"E6");var subQ2=makeQuery(id+"F0.imprint","INTERSECT",VERTEX,{"derivedFrom":[subQ1,subQ0]});Q64=makeQuery(id+"F0.imprint","IMPRINT",FACE,{"disambiguationData":[TD([[makeQuery(id+"F0.imprint","IMPRINT",EDGE,{"disambiguationData":[TD([[subQ2,1.0]])],"derivedFrom":subQ1}),-1.0]])]});}
            var Q65;
            {var subQ0=sQuery(id+"F0.wireOp",EDGE,"E10.1.3");var subQ1=sQuery(id+"F0.wireOp",EDGE,"E6");var subQ2=makeQuery(id+"F0.imprint","INTERSECT",VERTEX,{"derivedFrom":[subQ1,subQ0]});Q65=makeQuery(id+"F0.imprint","IMPRINT",FACE,{"disambiguationData":[TD([[makeQuery(id+"F0.imprint","IMPRINT",EDGE,{"disambiguationData":[TD([[subQ2,-1.0]])],"derivedFrom":subQ1}),-1.0]])]});}
            var Q66;
            {var subQ0=sQuery(id+"F0.wireOp",EDGE,"E10.7.2");var subQ1=sQuery(id+"F0.wireOp",EDGE,"E6");var subQ2=makeQuery(id+"F0.imprint","INTERSECT",VERTEX,{"derivedFrom":[subQ1,subQ0]});Q66=makeQuery(id+"F0.imprint","IMPRINT",FACE,{"disambiguationData":[TD([[makeQuery(id+"F0.imprint","IMPRINT",EDGE,{"disambiguationData":[TD([[subQ2,1.0]])],"derivedFrom":subQ1}),-1.0]])]});}
            var Q67;
            {var subQ0=sQuery(id+"F0.wireOp",EDGE,"E10.2.3");var subQ1=sQuery(id+"F0.wireOp",EDGE,"E6");var subQ2=makeQuery(id+"F0.imprint","INTERSECT",VERTEX,{"derivedFrom":[subQ1,subQ0]});Q67=makeQuery(id+"F0.imprint","IMPRINT",FACE,{"disambiguationData":[TD([[makeQuery(id+"F0.imprint","IMPRINT",EDGE,{"disambiguationData":[TD([[subQ2,-1.0]])],"derivedFrom":subQ1}),-1.0]])]});}
            var Q68;
            {var subQ0=sQuery(id+"F0.wireOp",EDGE,"E6");var subQ1=sQuery(id+"F0.wireOp",EDGE,"E0");var subQ2=makeQuery(id+"F0.imprint","INTERSECT",VERTEX,{"derivedFrom":[subQ1,subQ0]});Q68=makeQuery(id+"F0.imprint","IMPRINT",FACE,{"disambiguationData":[TD([[makeQuery(id+"F0.imprint","IMPRINT",EDGE,{"disambiguationData":[TD([[subQ2,1.0]])],"derivedFrom":subQ0}),-1.0]])]});}
            var Q69;
            {var subQ0=sQuery(id+"F0.wireOp",EDGE,"E10.3.3");var subQ1=sQuery(id+"F0.wireOp",EDGE,"E6");var subQ2=makeQuery(id+"F0.imprint","INTERSECT",VERTEX,{"derivedFrom":[subQ1,subQ0]});Q69=makeQuery(id+"F0.imprint","IMPRINT",FACE,{"disambiguationData":[TD([[makeQuery(id+"F0.imprint","IMPRINT",EDGE,{"disambiguationData":[TD([[subQ2,-1.0]])],"derivedFrom":subQ1}),-1.0]])]});}
            var Q70;
            {var subQ0=sQuery(id+"F0.wireOp",EDGE,"E10.4.3");var subQ1=sQuery(id+"F0.wireOp",EDGE,"E6");var subQ2=makeQuery(id+"F0.imprint","INTERSECT",VERTEX,{"derivedFrom":[subQ1,subQ0]});Q70=makeQuery(id+"F0.imprint","IMPRINT",FACE,{"disambiguationData":[TD([[makeQuery(id+"F0.imprint","IMPRINT",EDGE,{"disambiguationData":[TD([[subQ2,-1.0]])],"derivedFrom":subQ1}),-1.0]])]});}
            var Q71;
            {var subQ0=sQuery(id+"F0.wireOp",EDGE,"E10.2.2");var subQ1=sQuery(id+"F0.wireOp",EDGE,"E6");var subQ2=makeQuery(id+"F0.imprint","INTERSECT",VERTEX,{"derivedFrom":[subQ1,subQ0]});Q71=makeQuery(id+"F0.imprint","IMPRINT",FACE,{"disambiguationData":[TD([[makeQuery(id+"F0.imprint","IMPRINT",EDGE,{"disambiguationData":[TD([[subQ2,1.0]])],"derivedFrom":subQ1}),-1.0]])]});}
            var Q72;
            {var subQ0=sQuery(id+"F0.wireOp",EDGE,"E10.3.2");var subQ1=sQuery(id+"F0.wireOp",EDGE,"E6");var subQ2=makeQuery(id+"F0.imprint","INTERSECT",VERTEX,{"derivedFrom":[subQ1,subQ0]});Q72=makeQuery(id+"F0.imprint","IMPRINT",FACE,{"disambiguationData":[TD([[makeQuery(id+"F0.imprint","IMPRINT",EDGE,{"disambiguationData":[TD([[subQ2,1.0]])],"derivedFrom":subQ1}),-1.0]])]});}
            var Q73;
            {var subQ0=sQuery(id+"F0.wireOp",EDGE,"E10.5.3");var subQ1=sQuery(id+"F0.wireOp",EDGE,"E6");var subQ2=makeQuery(id+"F0.imprint","INTERSECT",VERTEX,{"derivedFrom":[subQ1,subQ0]});Q73=makeQuery(id+"F0.imprint","IMPRINT",FACE,{"disambiguationData":[TD([[makeQuery(id+"F0.imprint","IMPRINT",EDGE,{"disambiguationData":[TD([[subQ2,-1.0]])],"derivedFrom":subQ1}),-1.0]])]});}
            var Q74;
            {var subQ12=sQuery(id+"F0.wireOp",EDGE,"E6");var subQ14=sQuery(id+"F0.wireOp",EDGE,"E10.1.2");var subQ15=makeQuery(id+"F0.imprint","INTERSECT",VERTEX,{"derivedFrom":[subQ12,subQ14]});Q74=makeQuery(id+"F0.imprint","IMPRINT",FACE,{"disambiguationData":[TD([[makeQuery(id+"F0.imprint","IMPRINT",EDGE,{"disambiguationData":[TD([[subQ15,-1.0]])],"derivedFrom":subQ12}),-1.0]])]});}
            var Q75;
            {var subQ0=sQuery(id+"F0.wireOp",EDGE,"E10.1.2");var subQ1=sQuery(id+"F0.wireOp",EDGE,"E6");var subQ2=makeQuery(id+"F0.imprint","INTERSECT",VERTEX,{"derivedFrom":[subQ1,subQ0]});Q75=makeQuery(id+"F0.imprint","IMPRINT",FACE,{"disambiguationData":[TD([[makeQuery(id+"F0.imprint","IMPRINT",EDGE,{"disambiguationData":[TD([[subQ2,1.0]])],"derivedFrom":subQ1}),-1.0]])]});}
            var Q76;
            {var subQ0=sQuery(id+"F0.wireOp",EDGE,"E10.5.2");var subQ1=sQuery(id+"F0.wireOp",EDGE,"E6");var subQ2=makeQuery(id+"F0.imprint","INTERSECT",VERTEX,{"derivedFrom":[subQ1,subQ0]});Q76=makeQuery(id+"F0.imprint","IMPRINT",FACE,{"disambiguationData":[TD([[makeQuery(id+"F0.imprint","IMPRINT",EDGE,{"disambiguationData":[TD([[subQ2,1.0]])],"derivedFrom":subQ1}),-1.0]])]});}
            var Q77;
            {var subQ0=sQuery(id+"F0.wireOp",EDGE,"E10.7.3");var subQ1=sQuery(id+"F0.wireOp",EDGE,"E6");var subQ2=makeQuery(id+"F0.imprint","INTERSECT",VERTEX,{"derivedFrom":[subQ1,subQ0]});Q77=makeQuery(id+"F0.imprint","IMPRINT",FACE,{"disambiguationData":[TD([[makeQuery(id+"F0.imprint","IMPRINT",EDGE,{"disambiguationData":[TD([[subQ2,-1.0]])],"derivedFrom":subQ1}),-1.0]])]});}
            var Q78;
            {var subQ0=sQuery(id+"F0.wireOp",EDGE,"E10.6.3");var subQ1=sQuery(id+"F0.wireOp",EDGE,"E6");var subQ2=makeQuery(id+"F0.imprint","INTERSECT",VERTEX,{"derivedFrom":[subQ1,subQ0]});Q78=makeQuery(id+"F0.imprint","IMPRINT",FACE,{"disambiguationData":[TD([[makeQuery(id+"F0.imprint","IMPRINT",EDGE,{"disambiguationData":[TD([[subQ2,-1.0]])],"derivedFrom":subQ1}),-1.0]])]});}
            var Q79;
            {var subQ0=sQuery(id+"F0.wireOp",EDGE,"E10.4.2");var subQ1=sQuery(id+"F0.wireOp",EDGE,"E6");var subQ2=makeQuery(id+"F0.imprint","INTERSECT",VERTEX,{"derivedFrom":[subQ1,subQ0]});Q79=makeQuery(id+"F0.imprint","IMPRINT",FACE,{"disambiguationData":[TD([[makeQuery(id+"F0.imprint","IMPRINT",EDGE,{"disambiguationData":[TD([[subQ2,1.0]])],"derivedFrom":subQ1}),-1.0]])]});}
            extrude(context, id + "F1", {"entities" : qUnion([Q0, Q1, Q2, Q3, Q4, Q5, Q6, Q7, Q8, Q9, Q10, Q11, Q12, Q13, Q14, Q15, Q16, Q17, Q18, Q19, Q20, Q21, Q22, Q23, Q24, Q25, Q26, Q27, Q28, Q29, Q30, Q31, Q32, Q33, Q34, Q35, Q36, Q37, Q38, Q39, Q40, Q41, Q42, Q43, Q44, Q45, Q46, Q47, Q48, Q49, Q50, Q51, Q52, Q53, Q54, Q55, Q56, Q57, Q58, Q59, Q60, Q61, Q62, Q63, Q64, Q65, Q66, Q67, Q68, Q69, Q70, Q71, Q72, Q73, Q74, Q75, Q76, Q77, Q78, Q79]), "depth" : 7 * mm, "offsetDistance" : 25.4 * mm});
        }
        {
            var Q0;
            Q0=makeQuery(id+"F1.opExtrude","CAP_FACE",FACE,{"disambiguationData":[OSD([sQuery(id+"F0.wireOp",EDGE,"E1"),sQuery(id+"F0.wireOp",EDGE,"E2"),sQuery(id+"F0.wireOp",EDGE,"E3"),sQuery(id+"F0.wireOp",EDGE,"E6"),sQuery(id+"F0.wireOp",EDGE,"E9"),sQuery(id+"F0.wireOp",EDGE,"E10.1.0"),sQuery(id+"F0.wireOp",EDGE,"E10.1.4"),sQuery(id+"F0.wireOp",EDGE,"E10.1.7"),sQuery(id+"F0.wireOp",EDGE,"E10.1.8"),sQuery(id+"F0.wireOp",EDGE,"E10.2.0"),sQuery(id+"F0.wireOp",EDGE,"E10.2.4"),sQuery(id+"F0.wireOp",EDGE,"E10.2.7"),sQuery(id+"F0.wireOp",EDGE,"E10.2.8"),sQuery(id+"F0.wireOp",EDGE,"E10.3.0"),sQuery(id+"F0.wireOp",EDGE,"E10.3.4"),sQuery(id+"F0.wireOp",EDGE,"E10.3.7"),sQuery(id+"F0.wireOp",EDGE,"E10.3.8"),sQuery(id+"F0.wireOp",EDGE,"E10.4.0"),sQuery(id+"F0.wireOp",EDGE,"E10.4.4"),sQuery(id+"F0.wireOp",EDGE,"E10.4.7"),sQuery(id+"F0.wireOp",EDGE,"E10.4.8"),sQuery(id+"F0.wireOp",EDGE,"E10.5.0"),sQuery(id+"F0.wireOp",EDGE,"E10.5.4"),sQuery(id+"F0.wireOp",EDGE,"E10.5.7"),sQuery(id+"F0.wireOp",EDGE,"E10.5.8"),sQuery(id+"F0.wireOp",EDGE,"E10.6.0"),sQuery(id+"F0.wireOp",EDGE,"E10.6.4"),sQuery(id+"F0.wireOp",EDGE,"E10.6.7"),sQuery(id+"F0.wireOp",EDGE,"E10.6.8"),sQuery(id+"F0.wireOp",EDGE,"E10.7.0"),sQuery(id+"F0.wireOp",EDGE,"E10.7.4"),sQuery(id+"F0.wireOp",EDGE,"E10.7.7"),sQuery(id+"F0.wireOp",EDGE,"E10.7.8")])],"isStart":false});
            var Q1;
            Q1=makeQuery(id+"F1.opExtrude","CAP_FACE",FACE,{"disambiguationData":[OSD([sQuery(id+"F0.wireOp",EDGE,"E1"),sQuery(id+"F0.wireOp",EDGE,"E2"),sQuery(id+"F0.wireOp",EDGE,"E3"),sQuery(id+"F0.wireOp",EDGE,"E6"),sQuery(id+"F0.wireOp",EDGE,"E9"),sQuery(id+"F0.wireOp",EDGE,"E10.1.0"),sQuery(id+"F0.wireOp",EDGE,"E10.1.4"),sQuery(id+"F0.wireOp",EDGE,"E10.1.7"),sQuery(id+"F0.wireOp",EDGE,"E10.1.8"),sQuery(id+"F0.wireOp",EDGE,"E10.2.0"),sQuery(id+"F0.wireOp",EDGE,"E10.2.4"),sQuery(id+"F0.wireOp",EDGE,"E10.2.7"),sQuery(id+"F0.wireOp",EDGE,"E10.2.8"),sQuery(id+"F0.wireOp",EDGE,"E10.3.0"),sQuery(id+"F0.wireOp",EDGE,"E10.3.4"),sQuery(id+"F0.wireOp",EDGE,"E10.3.7"),sQuery(id+"F0.wireOp",EDGE,"E10.3.8"),sQuery(id+"F0.wireOp",EDGE,"E10.4.0"),sQuery(id+"F0.wireOp",EDGE,"E10.4.4"),sQuery(id+"F0.wireOp",EDGE,"E10.4.7"),sQuery(id+"F0.wireOp",EDGE,"E10.4.8"),sQuery(id+"F0.wireOp",EDGE,"E10.5.0"),sQuery(id+"F0.wireOp",EDGE,"E10.5.4"),sQuery(id+"F0.wireOp",EDGE,"E10.5.7"),sQuery(id+"F0.wireOp",EDGE,"E10.5.8"),sQuery(id+"F0.wireOp",EDGE,"E10.6.0"),sQuery(id+"F0.wireOp",EDGE,"E10.6.4"),sQuery(id+"F0.wireOp",EDGE,"E10.6.7"),sQuery(id+"F0.wireOp",EDGE,"E10.6.8"),sQuery(id+"F0.wireOp",EDGE,"E10.7.0"),sQuery(id+"F0.wireOp",EDGE,"E10.7.4"),sQuery(id+"F0.wireOp",EDGE,"E10.7.7"),sQuery(id+"F0.wireOp",EDGE,"E10.7.8")])],"isStart":true});
            shell(context, id + "F2", {"entities" : qUnion([Q0, Q1]), "thickness" : 5.6 * mm});
        }
        {
            var Q0;
            Q0=makeQuery(id+"F1.opExtrude","CAP_EDGE",EDGE,{"disambiguationData":[OSD([sQuery(id+"F0.wireOp",EDGE,"E10.1.7")])],"isStart":false});
            var Q1;
            Q1=makeQuery(id+"F1.opExtrude","CAP_EDGE",EDGE,{"disambiguationData":[OSD([sQuery(id+"F0.wireOp",EDGE,"E10.1.8")])],"isStart":false});
            var Q2;
            Q2=makeQuery(id+"F1.opExtrude","CAP_EDGE",EDGE,{"disambiguationData":[OSD([sQuery(id+"F0.wireOp",EDGE,"E1")])],"isStart":false});
            var Q3;
            Q3=makeQuery(id+"F1.opExtrude","CAP_EDGE",EDGE,{"disambiguationData":[OSD([sQuery(id+"F0.wireOp",EDGE,"E2")])],"isStart":false});
            var Q4;
            Q4=makeQuery(id+"F1.opExtrude","CAP_EDGE",EDGE,{"disambiguationData":[OSD([sQuery(id+"F0.wireOp",EDGE,"E3")])],"isStart":false});
            var Q5;
            Q5=makeQuery(id+"F1.opExtrude","CAP_EDGE",EDGE,{"disambiguationData":[OSD([sQuery(id+"F0.wireOp",EDGE,"E10.7.0")])],"isStart":false});
            var Q6;
            Q6=makeQuery(id+"F1.opExtrude","CAP_EDGE",EDGE,{"disambiguationData":[OSD([sQuery(id+"F0.wireOp",EDGE,"E10.7.7")])],"isStart":false});
            var Q7;
            Q7=makeQuery(id+"F1.opExtrude","CAP_EDGE",EDGE,{"disambiguationData":[OSD([sQuery(id+"F0.wireOp",EDGE,"E10.7.8")])],"isStart":false});
            var Q8;
            Q8=makeQuery(id+"F1.opExtrude","CAP_EDGE",EDGE,{"disambiguationData":[OSD([sQuery(id+"F0.wireOp",EDGE,"E10.6.0")])],"isStart":false});
            var Q9;
            Q9=makeQuery(id+"F1.opExtrude","CAP_EDGE",EDGE,{"disambiguationData":[OSD([sQuery(id+"F0.wireOp",EDGE,"E10.6.7")])],"isStart":false});
            var Q10;
            Q10=makeQuery(id+"F1.opExtrude","CAP_EDGE",EDGE,{"disambiguationData":[OSD([sQuery(id+"F0.wireOp",EDGE,"E10.6.8")])],"isStart":false});
            var Q11;
            Q11=makeQuery(id+"F1.opExtrude","CAP_EDGE",EDGE,{"disambiguationData":[OSD([sQuery(id+"F0.wireOp",EDGE,"E10.5.0")])],"isStart":false});
            var Q12;
            Q12=makeQuery(id+"F1.opExtrude","CAP_EDGE",EDGE,{"disambiguationData":[OSD([sQuery(id+"F0.wireOp",EDGE,"E10.5.7")])],"isStart":false});
            var Q13;
            Q13=makeQuery(id+"F1.opExtrude","CAP_EDGE",EDGE,{"disambiguationData":[OSD([sQuery(id+"F0.wireOp",EDGE,"E10.5.8")])],"isStart":false});
            var Q14;
            Q14=makeQuery(id+"F1.opExtrude","CAP_EDGE",EDGE,{"disambiguationData":[OSD([sQuery(id+"F0.wireOp",EDGE,"E10.4.0")])],"isStart":false});
            var Q15;
            Q15=makeQuery(id+"F1.opExtrude","CAP_EDGE",EDGE,{"disambiguationData":[OSD([sQuery(id+"F0.wireOp",EDGE,"E10.4.7")])],"isStart":false});
            var Q16;
            Q16=makeQuery(id+"F1.opExtrude","CAP_EDGE",EDGE,{"disambiguationData":[OSD([sQuery(id+"F0.wireOp",EDGE,"E10.4.8")])],"isStart":false});
            var Q17;
            Q17=makeQuery(id+"F1.opExtrude","CAP_EDGE",EDGE,{"disambiguationData":[OSD([sQuery(id+"F0.wireOp",EDGE,"E10.3.0")])],"isStart":false});
            var Q18;
            Q18=makeQuery(id+"F1.opExtrude","CAP_EDGE",EDGE,{"disambiguationData":[OSD([sQuery(id+"F0.wireOp",EDGE,"E10.3.7")])],"isStart":false});
            var Q19;
            Q19=makeQuery(id+"F1.opExtrude","CAP_EDGE",EDGE,{"disambiguationData":[OSD([sQuery(id+"F0.wireOp",EDGE,"E10.3.8")])],"isStart":false});
            var Q20;
            Q20=makeQuery(id+"F1.opExtrude","CAP_EDGE",EDGE,{"disambiguationData":[OSD([sQuery(id+"F0.wireOp",EDGE,"E10.2.0")])],"isStart":false});
            var Q21;
            Q21=makeQuery(id+"F1.opExtrude","CAP_EDGE",EDGE,{"disambiguationData":[OSD([sQuery(id+"F0.wireOp",EDGE,"E10.2.7")])],"isStart":false});
            var Q22;
            Q22=makeQuery(id+"F1.opExtrude","CAP_EDGE",EDGE,{"disambiguationData":[OSD([sQuery(id+"F0.wireOp",EDGE,"E10.2.8")])],"isStart":false});
            var Q23;
            Q23=makeQuery(id+"F1.opExtrude","CAP_EDGE",EDGE,{"disambiguationData":[OSD([sQuery(id+"F0.wireOp",EDGE,"E10.1.0")])],"isStart":false});
            chamfer(context, id + "F3", {"entities" : qUnion([Q0, Q1, Q2, Q3, Q4, Q5, Q6, Q7, Q8, Q9, Q10, Q11, Q12, Q13, Q14, Q15, Q16, Q17, Q18, Q19, Q20, Q21, Q22, Q23]), "width" : 1.27 * mm, "tangentPropagation" : true});
        }
        {
            var Q0;
            Q0=makeQuery(id+"F1.opExtrude","CAP_EDGE",EDGE,{"disambiguationData":[OSD([sQuery(id+"F0.wireOp",EDGE,"E10.1.7")])],"isStart":true});
            var Q1;
            Q1=makeQuery(id+"F1.opExtrude","CAP_EDGE",EDGE,{"disambiguationData":[OSD([sQuery(id+"F0.wireOp",EDGE,"E10.1.0")])],"isStart":true});
            var Q2;
            Q2=makeQuery(id+"F1.opExtrude","CAP_EDGE",EDGE,{"disambiguationData":[OSD([sQuery(id+"F0.wireOp",EDGE,"E10.2.8")])],"isStart":true});
            var Q3;
            Q3=makeQuery(id+"F1.opExtrude","CAP_EDGE",EDGE,{"disambiguationData":[OSD([sQuery(id+"F0.wireOp",EDGE,"E10.2.7")])],"isStart":true});
            var Q4;
            Q4=makeQuery(id+"F1.opExtrude","CAP_EDGE",EDGE,{"disambiguationData":[OSD([sQuery(id+"F0.wireOp",EDGE,"E10.3.8")])],"isStart":true});
            var Q5;
            Q5=makeQuery(id+"F1.opExtrude","CAP_EDGE",EDGE,{"disambiguationData":[OSD([sQuery(id+"F0.wireOp",EDGE,"E10.2.0")])],"isStart":true});
            var Q6;
            Q6=makeQuery(id+"F1.opExtrude","CAP_EDGE",EDGE,{"disambiguationData":[OSD([sQuery(id+"F0.wireOp",EDGE,"E10.3.7")])],"isStart":true});
            var Q7;
            Q7=makeQuery(id+"F1.opExtrude","CAP_EDGE",EDGE,{"disambiguationData":[OSD([sQuery(id+"F0.wireOp",EDGE,"E10.3.0")])],"isStart":true});
            var Q8;
            Q8=makeQuery(id+"F1.opExtrude","CAP_EDGE",EDGE,{"disambiguationData":[OSD([sQuery(id+"F0.wireOp",EDGE,"E10.4.8")])],"isStart":true});
            var Q9;
            Q9=makeQuery(id+"F1.opExtrude","CAP_EDGE",EDGE,{"disambiguationData":[OSD([sQuery(id+"F0.wireOp",EDGE,"E10.4.7")])],"isStart":true});
            var Q10;
            Q10=makeQuery(id+"F1.opExtrude","CAP_EDGE",EDGE,{"disambiguationData":[OSD([sQuery(id+"F0.wireOp",EDGE,"E10.4.0")])],"isStart":true});
            var Q11;
            Q11=makeQuery(id+"F1.opExtrude","CAP_EDGE",EDGE,{"disambiguationData":[OSD([sQuery(id+"F0.wireOp",EDGE,"E10.5.8")])],"isStart":true});
            var Q12;
            Q12=makeQuery(id+"F1.opExtrude","CAP_EDGE",EDGE,{"disambiguationData":[OSD([sQuery(id+"F0.wireOp",EDGE,"E10.5.7")])],"isStart":true});
            var Q13;
            Q13=makeQuery(id+"F1.opExtrude","CAP_EDGE",EDGE,{"disambiguationData":[OSD([sQuery(id+"F0.wireOp",EDGE,"E10.5.0")])],"isStart":true});
            var Q14;
            Q14=makeQuery(id+"F1.opExtrude","CAP_EDGE",EDGE,{"disambiguationData":[OSD([sQuery(id+"F0.wireOp",EDGE,"E10.6.8")])],"isStart":true});
            var Q15;
            Q15=makeQuery(id+"F1.opExtrude","CAP_EDGE",EDGE,{"disambiguationData":[OSD([sQuery(id+"F0.wireOp",EDGE,"E10.6.7")])],"isStart":true});
            var Q16;
            Q16=makeQuery(id+"F1.opExtrude","CAP_EDGE",EDGE,{"disambiguationData":[OSD([sQuery(id+"F0.wireOp",EDGE,"E10.7.8")])],"isStart":true});
            var Q17;
            Q17=makeQuery(id+"F1.opExtrude","CAP_EDGE",EDGE,{"disambiguationData":[OSD([sQuery(id+"F0.wireOp",EDGE,"E10.6.0")])],"isStart":true});
            var Q18;
            Q18=makeQuery(id+"F1.opExtrude","CAP_EDGE",EDGE,{"disambiguationData":[OSD([sQuery(id+"F0.wireOp",EDGE,"E10.7.7")])],"isStart":true});
            var Q19;
            Q19=makeQuery(id+"F1.opExtrude","CAP_EDGE",EDGE,{"disambiguationData":[OSD([sQuery(id+"F0.wireOp",EDGE,"E10.7.0")])],"isStart":true});
            var Q20;
            Q20=makeQuery(id+"F1.opExtrude","CAP_EDGE",EDGE,{"disambiguationData":[OSD([sQuery(id+"F0.wireOp",EDGE,"E3")])],"isStart":true});
            var Q21;
            Q21=makeQuery(id+"F1.opExtrude","CAP_EDGE",EDGE,{"disambiguationData":[OSD([sQuery(id+"F0.wireOp",EDGE,"E2")])],"isStart":true});
            var Q22;
            Q22=makeQuery(id+"F1.opExtrude","CAP_EDGE",EDGE,{"disambiguationData":[OSD([sQuery(id+"F0.wireOp",EDGE,"E1")])],"isStart":true});
            var Q23;
            Q23=makeQuery(id+"F1.opExtrude","CAP_EDGE",EDGE,{"disambiguationData":[OSD([sQuery(id+"F0.wireOp",EDGE,"E10.1.8")])],"isStart":true});
            chamfer(context, id + "F4", {"entities" : qUnion([Q0, Q1, Q2, Q3, Q4, Q5, Q6, Q7, Q8, Q9, Q10, Q11, Q12, Q13, Q14, Q15, Q16, Q17, Q18, Q19, Q20, Q21, Q22, Q23]), "width" : 1.27 * mm, "tangentPropagation" : true});
        }
    });
